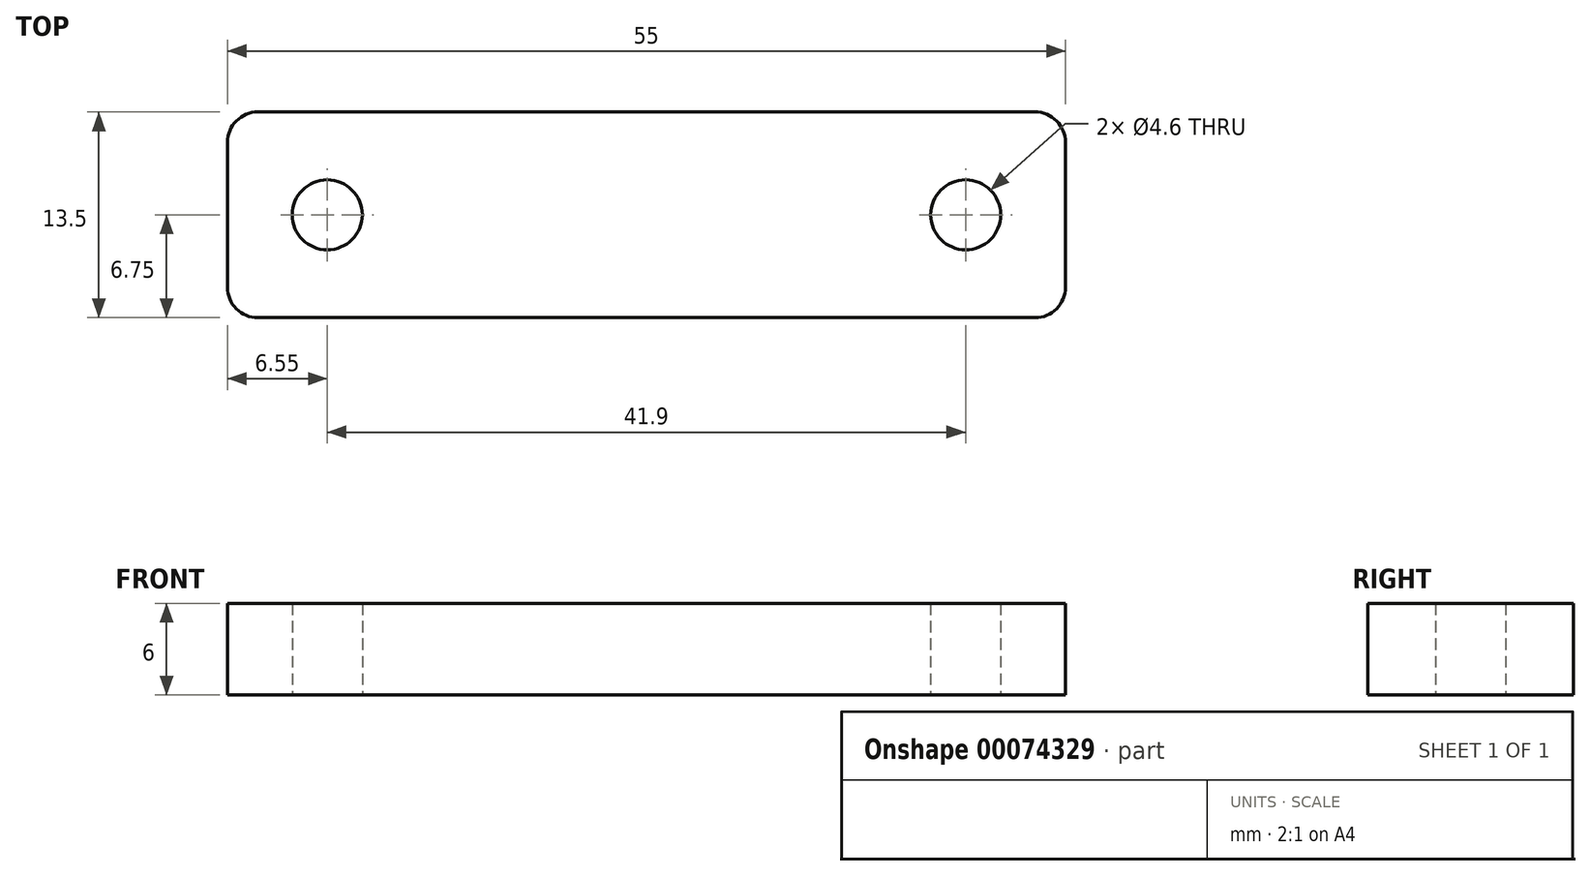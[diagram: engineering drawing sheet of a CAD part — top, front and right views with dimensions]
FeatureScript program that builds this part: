
annotation { "Feature Type Name" : "Feature", "Feature Type Description" : "" }
export const myFeature = defineFeature(function(context is Context, id is Id, definition is map)
    precondition{}
    {
        {
            var Q0;
            Q0=qCreatedBy(makeId("Top.planeOp"),FACE);
            var sketch = newSketch(context, id + "F0", { "sketchPlane" : qUnion([Q0])});
            skLineSegment(sketch, "E0.rect.bottom", {"start": v(27.5, 6.75) * mm, "end": v(-27.5, 6.75) * mm});
            skLineSegment(sketch, "E0.rect.top", {"start": v(27.5, -6.75) * mm, "end": v(-27.5, -6.75) * mm});
            skLineSegment(sketch, "E0.rect.left", {"start": v(27.5, 6.75) * mm, "end": v(27.5, -6.75) * mm});
            skLineSegment(sketch, "E0.rect.right", {"start": v(-27.5, 6.75) * mm, "end": v(-27.5, -6.75) * mm});
            skPoint(sketch, "E0.rect.middle", {"position": v(0, 0) * mm});
            skCircle(sketch, "E1", {"center": v(-20.95, 0) * mm, "radius": 2.3 * mm});
            skCircle(sketch, "E2.MirrorC", {"center": v(20.95, 0) * mm, "radius": 2.3 * mm});
            skSolve(sketch);
        }
        {
            var Q0;
            Q0=makeQuery(id+"F0.imprint","IMPRINT",FACE,{"disambiguationData":[TD([[makeQuery(id+"F0.imprint","IMPRINT",EDGE,{"derivedFrom":sQuery(id+"F0.wireOp",EDGE,"E0.rect.bottom")}),1.0]])]});
            extrude(context, id + "F1", {"entities" : qUnion([Q0]), "depth" : 6 * mm});
        }
        {
            var Q0;
            Q0=makeQuery(id+"F1.opExtrude","SWEPT_EDGE",EDGE,{"disambiguationData":[OSD([sQuery(id+"F0.wireOp",EDGE,"E0.rect.top"),sQuery(id+"F0.wireOp",EDGE,"E0.rect.right")])]});
            var Q1;
            Q1=makeQuery(id+"F1.opExtrude","SWEPT_EDGE",EDGE,{"disambiguationData":[OSD([sQuery(id+"F0.wireOp",EDGE,"E0.rect.bottom"),sQuery(id+"F0.wireOp",EDGE,"E0.rect.right")])]});
            var Q2;
            Q2=makeQuery(id+"F1.opExtrude","SWEPT_EDGE",EDGE,{"disambiguationData":[OSD([sQuery(id+"F0.wireOp",EDGE,"E0.rect.bottom"),sQuery(id+"F0.wireOp",EDGE,"E0.rect.left")])]});
            var Q3;
            Q3=makeQuery(id+"F1.opExtrude","SWEPT_EDGE",EDGE,{"disambiguationData":[OSD([sQuery(id+"F0.wireOp",EDGE,"E0.rect.top"),sQuery(id+"F0.wireOp",EDGE,"E0.rect.left")])]});
            fillet(context, id + "F2", {"entities" : qUnion([Q0, Q1, Q2, Q3]), "radius" : 2 * mm, "tangentPropagation" : true, "allowEdgeOverflow" : false});
        }
    });
